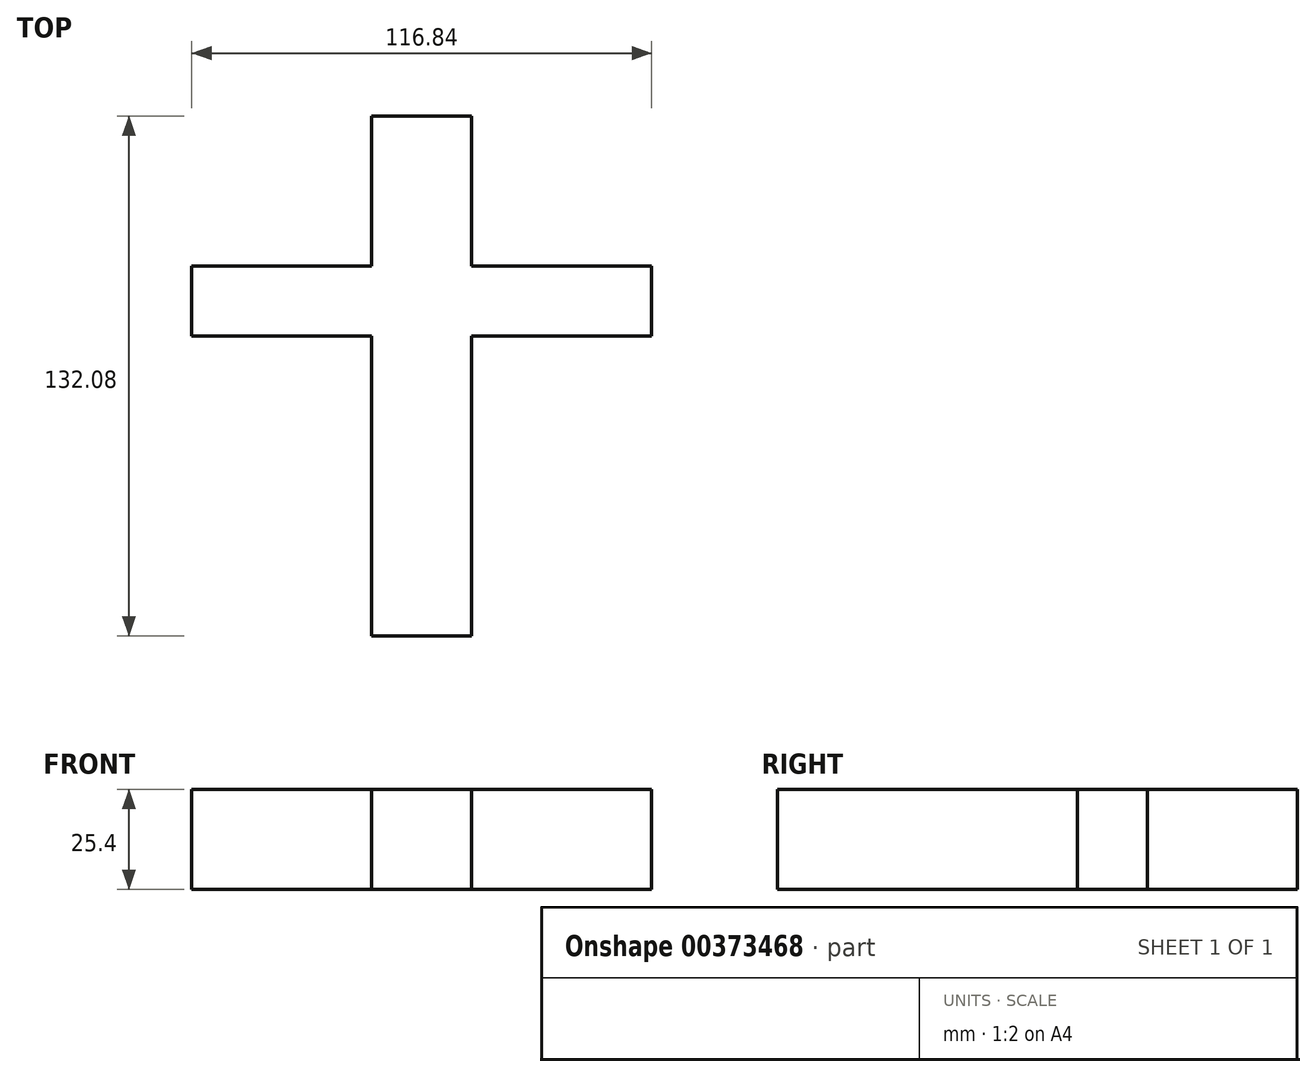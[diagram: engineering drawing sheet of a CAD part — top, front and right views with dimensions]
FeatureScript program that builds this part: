
annotation { "Feature Type Name" : "Feature", "Feature Type Description" : "" }
export const myFeature = defineFeature(function(context is Context, id is Id, definition is map)
    precondition{}
    {
        {
            var Q0;
            Q0=qCreatedBy(makeId("Top.planeOp"),FACE);
            var sketch = newSketch(context, id + "F0", { "sketchPlane" : qUnion([Q0])});
            skLineSegment(sketch, "E0", {"start": v(-15.1, 65.95) * mm, "end": v(10.3, 65.95) * mm});
            skLineSegment(sketch, "E1", {"start": v(10.3, 65.95) * mm, "end": v(10.3, 27.85) * mm});
            skLineSegment(sketch, "E2", {"start": v(10.3, 27.85) * mm, "end": v(56.03, 27.85) * mm});
            skLineSegment(sketch, "E3", {"start": v(56.03, 10.07) * mm, "end": v(56.03, 27.85) * mm});
            skLineSegment(sketch, "E4", {"start": v(56.03, 10.07) * mm, "end": v(10.3, 10.07) * mm});
            skLineSegment(sketch, "E5", {"start": v(10.3, 10.07) * mm, "end": v(10.3, -66.13) * mm});
            skLineSegment(sketch, "E6", {"start": v(10.3, -66.13) * mm, "end": v(-15.1, -66.13) * mm});
            skLineSegment(sketch, "E7", {"start": v(-15.1, -66.13) * mm, "end": v(-15.1, 10.07) * mm});
            skLineSegment(sketch, "E8", {"start": v(-15.1, 10.07) * mm, "end": v(-60.81, 10.07) * mm});
            skLineSegment(sketch, "E9", {"start": v(-60.81, 10.07) * mm, "end": v(-60.81, 27.85) * mm});
            skLineSegment(sketch, "E10", {"start": v(-60.81, 27.85) * mm, "end": v(-15.1, 27.85) * mm});
            skLineSegment(sketch, "E11", {"start": v(-15.1, 27.85) * mm, "end": v(-15.1, 65.95) * mm});
            skSolve(sketch);
        }
        {
            var Q0;
            Q0=makeQuery(id+"F0.imprint","IMPRINT",FACE,{"disambiguationData":[TD([[makeQuery(id+"F0.imprint","IMPRINT",EDGE,{"derivedFrom":sQuery(id+"F0.wireOp",EDGE,"E0")}),-1.0]])]});
            extrude(context, id + "F1", {"entities" : qUnion([Q0]), "depth" : 25.4 * mm});
        }
    });
